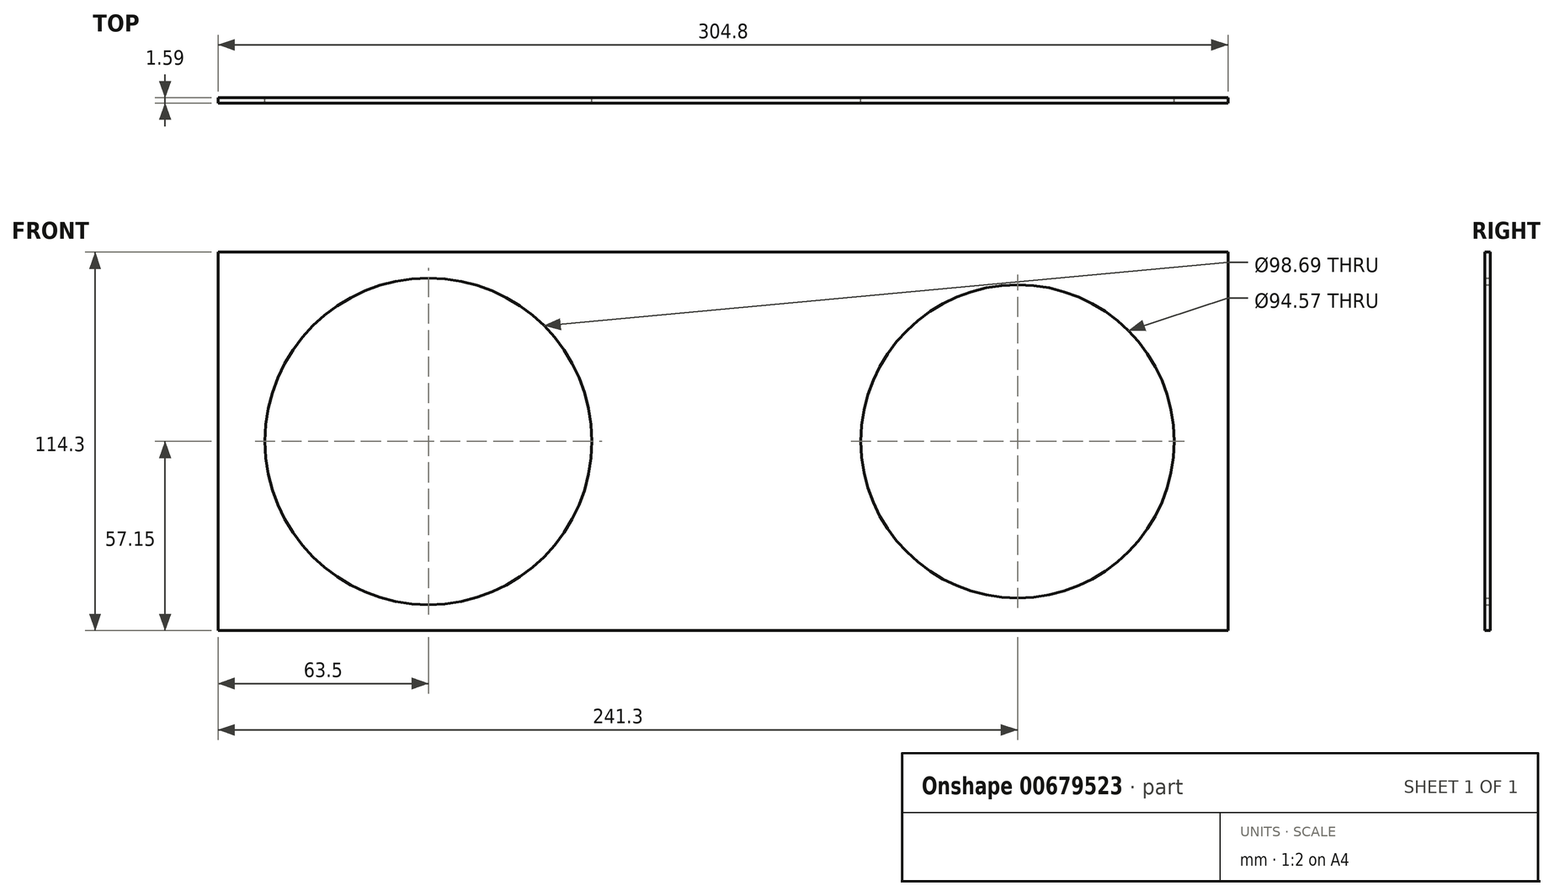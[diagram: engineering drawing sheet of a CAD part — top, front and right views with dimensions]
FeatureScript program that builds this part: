
annotation { "Feature Type Name" : "Feature", "Feature Type Description" : "" }
export const myFeature = defineFeature(function(context is Context, id is Id, definition is map)
    precondition{}
    {
        {
            var Q0;
            Q0=qCreatedBy(makeId("Front.planeOp"),FACE);
            var sketch = newSketch(context, id + "F0", { "sketchPlane" : qUnion([Q0])});
            skLineSegment(sketch, "E0.bottom", {"start": v(152.4, 57.15) * mm, "end": v(-152.4, 57.15) * mm});
            skLineSegment(sketch, "E0.top", {"start": v(152.4, -57.15) * mm, "end": v(-152.4, -57.15) * mm});
            skLineSegment(sketch, "E0.left", {"start": v(152.4, 57.15) * mm, "end": v(152.4, -57.15) * mm});
            skLineSegment(sketch, "E0.right", {"start": v(-152.4, 57.15) * mm, "end": v(-152.4, -57.15) * mm});
            skPoint(sketch, "E0.middle", {"position": v(0, 0) * mm});
            skLineSegment(sketch, "E1", {"start": v(-152.4, 0) * mm, "end": v(152.4, 0) * mm});
            skCircle(sketch, "E2", {"center": v(-88.9, 0) * mm, "radius": 49.34 * mm});
            skCircle(sketch, "E3", {"center": v(88.9, 0) * mm, "radius": 47.28 * mm});
            skSolve(sketch);
        }
        {
            var Q0;
            Q0 = qSketchRegion(id + "F0", true);
            extrude(context, id + "F1", {"entities" : qUnion([Q0]), "depth" : 1.59 * mm, "offsetDistance" : 25.4 * mm});
        }
    });
